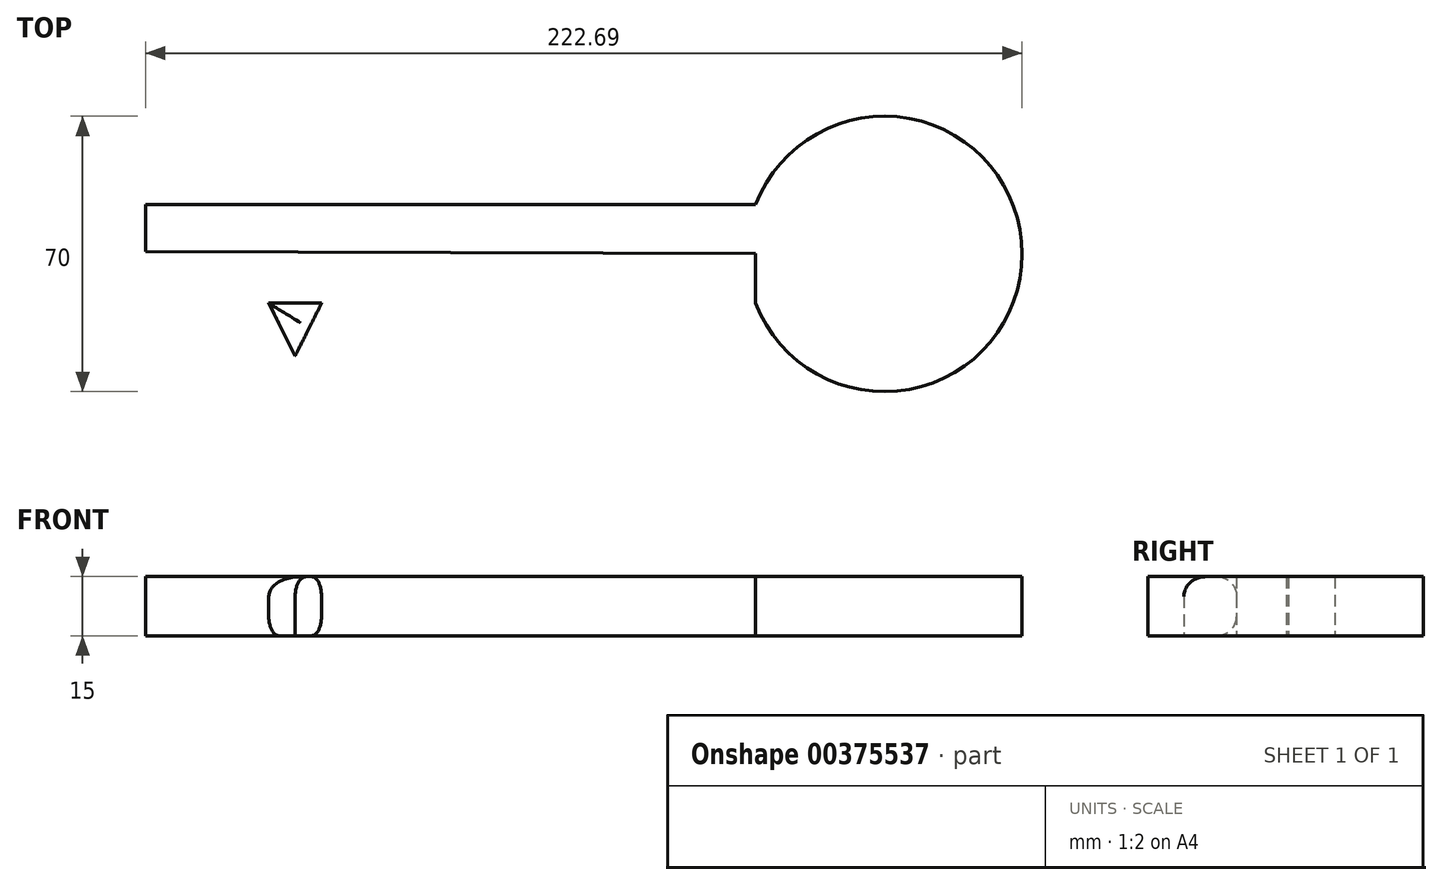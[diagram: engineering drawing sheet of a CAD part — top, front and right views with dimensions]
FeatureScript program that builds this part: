
annotation { "Feature Type Name" : "Feature", "Feature Type Description" : "" }
export const myFeature = defineFeature(function(context is Context, id is Id, definition is map)
    precondition{}
    {
        {
            var Q0;
            Q0=qCreatedBy(makeId("Top.planeOp"),FACE);
            var sketch = newSketch(context, id + "F0", { "sketchPlane" : qUnion([Q0])});
            skLineSegment(sketch, "E0.bottom", {"start": v(-38, 11.87) * mm, "end": v(117, 11.87) * mm});
            skLineSegment(sketch, "E0.top", {"start": v(-38, -13.13) * mm, "end": v(117, -13.13) * mm});
            skLineSegment(sketch, "E0.left", {"start": v(-38, 11.87) * mm, "end": v(-38, -13.13) * mm});
            skLineSegment(sketch, "E0.right", {"start": v(117, 11.87) * mm, "end": v(117, -13.13) * mm});
            skLineSegment(sketch, "E1.bottom", {"start": v(-38, -13.13) * mm, "end": v(-28, -13.13) * mm});
            skLineSegment(sketch, "E1.top", {"start": v(-38, -43.13) * mm, "end": v(-28, -43.13) * mm});
            skLineSegment(sketch, "E1.left", {"start": v(-38, -13.13) * mm, "end": v(-38, -43.13) * mm});
            skLineSegment(sketch, "E1.right", {"start": v(-28, -13.13) * mm, "end": v(-28, -43.13) * mm});
            skLineSegment(sketch, "E2.bottom", {"start": v(-10, -13.13) * mm, "end": v(-18, -13.13) * mm});
            skLineSegment(sketch, "E2.top", {"start": v(-10, -28.13) * mm, "end": v(-18, -28.13) * mm});
            skLineSegment(sketch, "E2.left", {"start": v(-10, -13.13) * mm, "end": v(-10, -28.13) * mm});
            skLineSegment(sketch, "E2.right", {"start": v(-18, -13.13) * mm, "end": v(-18, -28.13) * mm});
            skLineSegment(sketch, "E3", {"start": v(-6.7, -13.13) * mm, "end": v(0, -26.55) * mm});
            skLineSegment(sketch, "E4", {"start": v(0, -26.55) * mm, "end": v(6.7, -13.13) * mm});
            skArc(sketch, "E5", {"start": v(117, -13.13) * mm, "mid": v(184.7, -0.63) * mm, "end": v(117, 11.87) * mm});
            skCircle(sketch, "E6", {"center": v(149.7, -0.63) * mm, "radius": 17.5 * mm});
            skLineSegment(sketch, "E7", {"start": v(-38, 0) * mm, "end": v(149.7, -0.63) * mm});
            skSolve(sketch);
        }
        {
            var Q0;
            Q0=makeQuery(id+"F0.imprint","IMPRINT",FACE,{"disambiguationData":[TD([[makeQuery(id+"F0.imprint","IMPRINT",EDGE,{"derivedFrom":sQuery(id+"F0.wireOp",EDGE,"E6")}),1.0]])]});
            var Q1;
            {var subQ6=sQuery(id+"F0.wireOp",EDGE,"E1.bottom");Q1=makeQuery(id+"F0.imprint","IMPRINT",FACE,{"disambiguationData":[TD([[makeQuery(id+"F0.imprint","IMPRINT",EDGE,{"derivedFrom":subQ6}),1.0]])]});}
            var Q2;
            {var subQ0=sQuery(id+"F0.wireOp",EDGE,"E3");Q2=makeQuery(id+"F0.imprint","IMPRINT",FACE,{"disambiguationData":[TD([[makeQuery(id+"F0.imprint","IMPRINT",EDGE,{"derivedFrom":subQ0}),1.0]])]});}
            var Q3;
            Q3=makeQuery(id+"F0.imprint","IMPRINT",FACE,{"disambiguationData":[TD([[makeQuery(id+"F0.imprint","IMPRINT",EDGE,{"derivedFrom":sQuery(id+"F0.wireOp",EDGE,"E2.bottom")}),1.0]])]});
            var Q4;
            Q4=makeQuery(id+"F0.imprint","IMPRINT",FACE,{"disambiguationData":[TD([[makeQuery(id+"F0.imprint","IMPRINT",EDGE,{"derivedFrom":sQuery(id+"F0.wireOp",EDGE,"E1.bottom")}),-1.0]])]});
            var Q5;
            {var subQ0=sQuery(id+"F0.wireOp",EDGE,"E5");Q5=makeQuery(id+"F0.imprint","IMPRINT",FACE,{"disambiguationData":[TD([[makeQuery(id+"F0.imprint","IMPRINT",EDGE,{"derivedFrom":subQ0}),1.0]])]});}
            var Q6;
            {var subQ0=sQuery(id+"F0.wireOp",EDGE,"E0.bottom");Q6=makeQuery(id+"F0.imprint","IMPRINT",FACE,{"disambiguationData":[TD([[makeQuery(id+"F0.imprint","IMPRINT",EDGE,{"derivedFrom":subQ0}),-1.0]])]});}
            var Q7;
            Q7=sQuery(id+"F0.wireOp",EDGE,"E6");
            extrude(context, id + "F1", {"entities" : qUnion([Q0, Q1, Q2, Q3, Q4, Q5, Q6]), "surfaceEntities" : qUnion([Q7]), "depth" : 15 * mm});
        }
        {
            var Q0;
            Q0=makeQuery(id+"F1.opExtrude","CAP_EDGE",EDGE,{"disambiguationData":[OSD([sQuery(id+"F0.wireOp",EDGE,"E0.bottom")])],"isStart":false});
            var Q1;
            {var subQ0=sQuery(id+"F0.wireOp",EDGE,"E0.top");Q1=makeQuery(id+"F1.opExtrude","CAP_EDGE",EDGE,{"disambiguationData":[OSD([subQ0]),TDD([makeQuery(id+"F0.imprint","IMPRINT",EDGE,{"disambiguationData":[TD([[makeQuery(id+"F0.imprint","INTERSECT",VERTEX,{"derivedFrom":[subQ0,sQuery(id+"F0.wireOp",EDGE,"E4")]}),-1.0]])],"derivedFrom":subQ0})])],"isStart":false});}
            var Q2;
            Q2=makeQuery(id+"F1.opExtrude","CAP_EDGE",EDGE,{"disambiguationData":[OSD([sQuery(id+"F0.wireOp",EDGE,"E5")])],"isStart":false});
            var Q3;
            Q3=makeQuery(id+"F1.opExtrude","CAP_EDGE",EDGE,{"disambiguationData":[OSD([sQuery(id+"F0.wireOp",EDGE,"E3")])],"isStart":false});
            var Q4;
            {var subQ0=sQuery(id+"F0.wireOp",EDGE,"E0.top");Q4=makeQuery(id+"F1.opExtrude","CAP_EDGE",EDGE,{"disambiguationData":[OSD([subQ0]),TDD([makeQuery(id+"F0.imprint","IMPRINT",EDGE,{"disambiguationData":[TD([[makeQuery(id+"F0.imprint","INTERSECT",VERTEX,{"derivedFrom":[subQ0,sQuery(id+"F0.wireOp",EDGE,"E3")]}),1.0]])],"derivedFrom":subQ0})])],"isStart":false});}
            var Q5;
            Q5=makeQuery(id+"F1.opExtrude","CAP_EDGE",EDGE,{"disambiguationData":[OSD([sQuery(id+"F0.wireOp",EDGE,"E2.left")])],"isStart":false});
            var Q6;
            Q6=makeQuery(id+"F1.opExtrude","CAP_EDGE",EDGE,{"disambiguationData":[OSD([sQuery(id+"F0.wireOp",EDGE,"E1.top")])],"isStart":false});
            var Q7;
            Q7=makeQuery(id+"F1.opExtrude","CAP_EDGE",EDGE,{"disambiguationData":[OSD([sQuery(id+"F0.wireOp",EDGE,"E0.left"),sQuery(id+"F0.wireOp",EDGE,"E1.left")])],"isStart":false});
            var Q8;
            Q8=makeQuery(id+"F1.opExtrude","CAP_EDGE",EDGE,{"disambiguationData":[OSD([sQuery(id+"F0.wireOp",EDGE,"E0.bottom")])],"isStart":true});
            var Q9;
            Q9=makeQuery(id+"F1.opExtrude","CAP_EDGE",EDGE,{"disambiguationData":[OSD([sQuery(id+"F0.wireOp",EDGE,"E5")])],"isStart":true});
            var Q10;
            {var subQ0=sQuery(id+"F0.wireOp",EDGE,"E0.top");Q10=makeQuery(id+"F1.opExtrude","CAP_EDGE",EDGE,{"disambiguationData":[OSD([subQ0]),TDD([makeQuery(id+"F0.imprint","IMPRINT",EDGE,{"disambiguationData":[TD([[makeQuery(id+"F0.imprint","INTERSECT",VERTEX,{"derivedFrom":[subQ0,sQuery(id+"F0.wireOp",EDGE,"E4")]}),-1.0]])],"derivedFrom":subQ0})])],"isStart":true});}
            fillet(context, id + "F2", {"entities" : qUnion([Q0, Q1, Q2, Q3, Q4, Q5, Q6, Q7, Q8, Q9, Q10]), "radius" : 5 * mm, "tangentPropagation" : true, "allowEdgeOverflow" : false});
        }
    });
